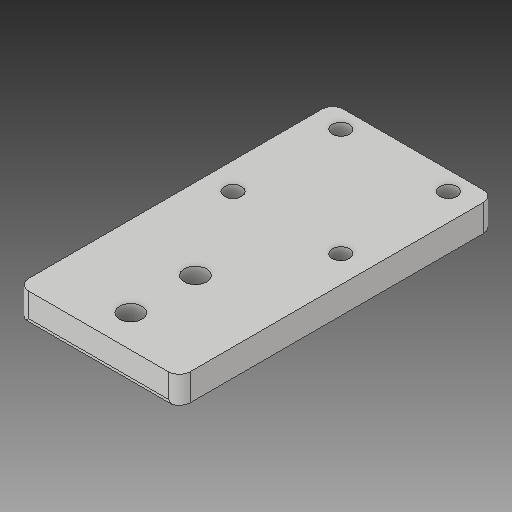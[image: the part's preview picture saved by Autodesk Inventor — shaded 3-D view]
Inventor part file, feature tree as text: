
AUTODESK INVENTOR PART (.ipt)
format: ipt  version: 2018 (Build 220112000, 112)  size: 122,368 bytes
history: native  units: in
note: dims shown in document units (in); Inventor stores cm internally (conversion verified against a paired STEP export)
features: sketch x6, other x3
ambient origin geometry x8: Origin, YZ Plane, XZ Plane, XY Plane, X Axis, Y Axis, Z Axis, Center Point
bodies: Solid1 (feature_tree)
feature tree (9):
  other  "X-connectorLeft.ipt"
  other  "Solid1::X-connectorLeft.ipt"
  other  "TaggingFeature1"
  sketch  "Sketch1"  dims[d0=0.3937in]
  sketch  "Sketch2"
  sketch  "Sketch3"
  sketch  "Sketch4"
  sketch  "Sketch5"
  sketch  "Sketch6"
